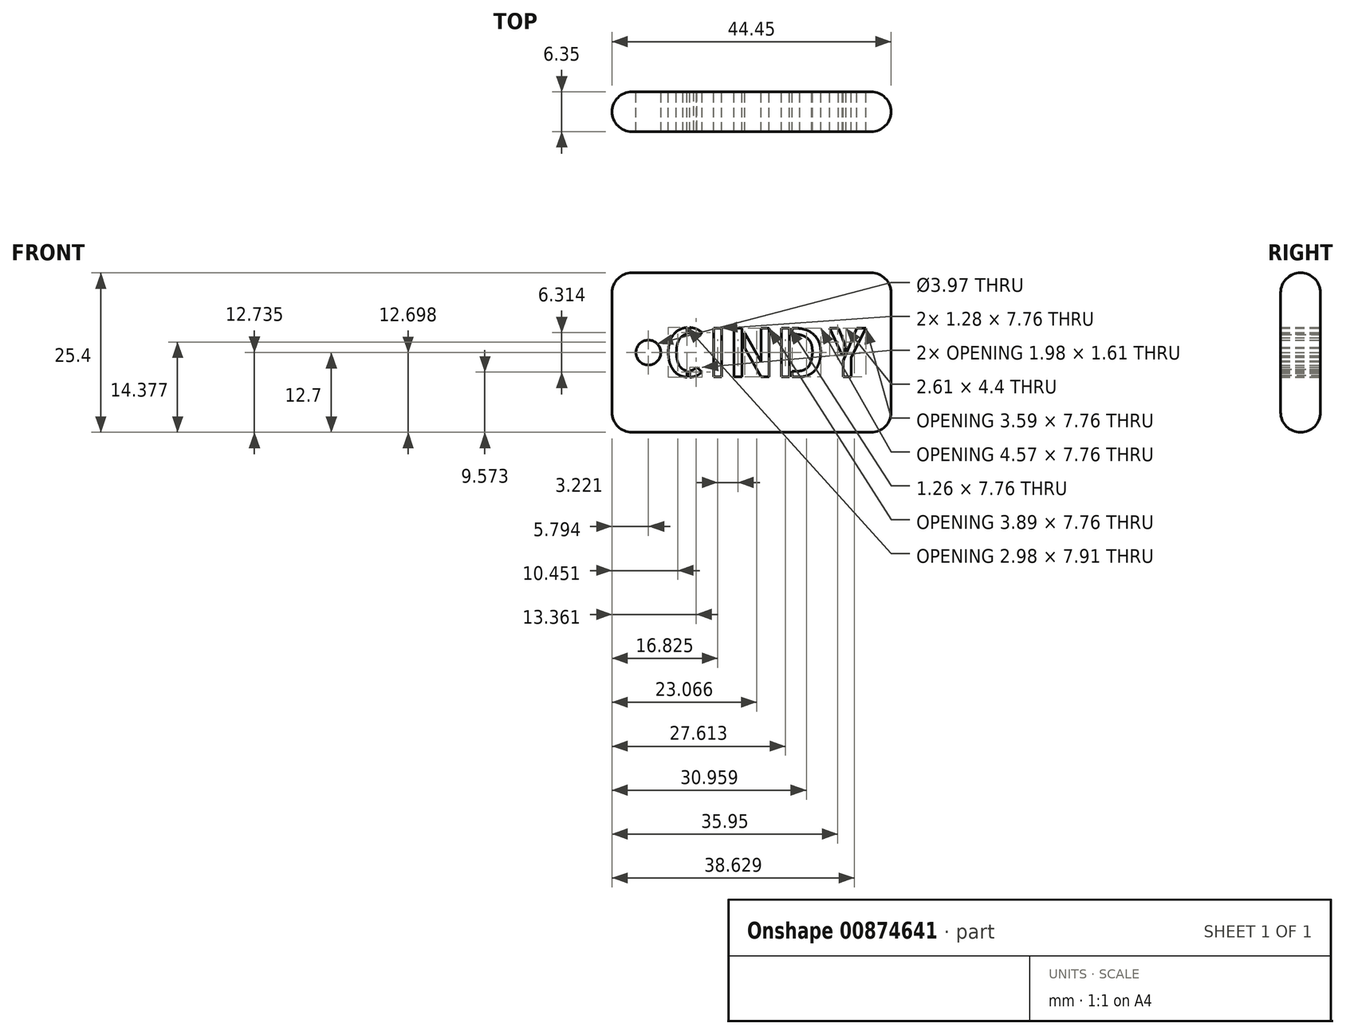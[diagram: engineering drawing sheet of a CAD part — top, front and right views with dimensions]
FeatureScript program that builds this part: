
annotation { "Feature Type Name" : "Feature", "Feature Type Description" : "" }
export const myFeature = defineFeature(function(context is Context, id is Id, definition is map)
    precondition{}
    {
        {
            var Q0;
            Q0=qCreatedBy(makeId("Front.planeOp"),FACE);
            var sketch = newSketch(context, id + "F0", { "sketchPlane" : qUnion([Q0])});
            skLineSegment(sketch, "E0.bottom", {"start": v(0, 0) * mm, "end": v(44.45, 0) * mm});
            skLineSegment(sketch, "E0.top", {"start": v(0, 25.4) * mm, "end": v(44.45, 25.4) * mm});
            skLineSegment(sketch, "E0.left", {"start": v(0, 0) * mm, "end": v(0, 25.4) * mm});
            skLineSegment(sketch, "E0.right", {"start": v(44.45, 0) * mm, "end": v(44.45, 25.4) * mm});
            skText(sketch, "E1", { "text": "CINDY\n", "fontName": "AllertaStencil-Regular.ttf"});
            skCircle(sketch, "E2", {"center": v(5.8, 12.7) * mm, "radius": 1.98 * mm});
            skPoint(sketch, "E3.visualSharp", {"position": v(44.45, 25.4) * mm});
            skLineSegment(sketch, "E3.filletArc", {"start": v(44.45, 25.4) * mm, "end": v(44.45, 25.4) * mm});
            skPoint(sketch, "E4.visualSharp", {"position": v(44.45, 0) * mm});
            skLineSegment(sketch, "E4.filletArc", {"start": v(44.45, 0) * mm, "end": v(44.45, 0) * mm});
            skPoint(sketch, "E5.visualSharp", {"position": v(0, 0) * mm});
            skLineSegment(sketch, "E5.filletArc", {"start": v(0, 0) * mm, "end": v(0, 0) * mm});
            skPoint(sketch, "E6.visualSharp", {"position": v(0, 25.4) * mm});
            skLineSegment(sketch, "E6.filletArc", {"start": v(0, 25.4) * mm, "end": v(0, 25.4) * mm});
            const initialGuessF0  = {"E1": [0.00813, 0.00882, 1, 0, 0.00776]};
            skSetInitialGuess(sketch, initialGuessF0);
            skSolve(sketch);
        }
        {
            var Q0;
            Q0=makeQuery(id+"F0.imprint","IMPRINT",FACE,{"disambiguationData":[TD([[makeQuery(id+"F0.imprint","IMPRINT",EDGE,{"derivedFrom":sQuery(id+"F0.wireOp",EDGE,"E0.bottom")}),1.0]])]});
            extrude(context, id + "F1", {"entities" : qUnion([Q0]), "depth" : 6.35 * mm, "offsetDistance" : 25.4 * mm});
        }
        {
            var Q0;
            Q0=makeQuery(id+"F1.opExtrude","CAP_EDGE",EDGE,{"disambiguationData":[OSD([sQuery(id+"F0.wireOp",EDGE,"E0.top")])],"isStart":false});
            var Q1;
            Q1=makeQuery(id+"F1.opExtrude","CAP_EDGE",EDGE,{"disambiguationData":[OSD([sQuery(id+"F0.wireOp",EDGE,"E0.bottom")])],"isStart":false});
            var Q2;
            Q2=makeQuery(id+"F1.opExtrude","CAP_EDGE",EDGE,{"disambiguationData":[OSD([sQuery(id+"F0.wireOp",EDGE,"E0.right")])],"isStart":false});
            var Q3;
            Q3=makeQuery(id+"F1.opExtrude","CAP_EDGE",EDGE,{"disambiguationData":[OSD([sQuery(id+"F0.wireOp",EDGE,"E0.left")])],"isStart":false});
            var Q4;
            Q4=makeQuery(id+"F1.opExtrude","CAP_EDGE",EDGE,{"disambiguationData":[OSD([sQuery(id+"F0.wireOp",EDGE,"E0.top")])],"isStart":true});
            var Q5;
            Q5=makeQuery(id+"F1.opExtrude","CAP_EDGE",EDGE,{"disambiguationData":[OSD([sQuery(id+"F0.wireOp",EDGE,"E0.right")])],"isStart":true});
            var Q6;
            Q6=makeQuery(id+"F1.opExtrude","CAP_EDGE",EDGE,{"disambiguationData":[OSD([sQuery(id+"F0.wireOp",EDGE,"E0.left")])],"isStart":true});
            var Q7;
            Q7=makeQuery(id+"F1.opExtrude","CAP_EDGE",EDGE,{"disambiguationData":[OSD([sQuery(id+"F0.wireOp",EDGE,"E0.bottom")])],"isStart":true});
            fillet(context, id + "F2", {"entities" : qUnion([Q0, Q1, Q2, Q3, Q4, Q5, Q6, Q7]), "radius" : 3.17 * mm, "tangentPropagation" : true, "allowEdgeOverflow" : false});
        }
        {
            var Q0;
            Q0=makeQuery(id+"F2.opFillet","BLEND_EDGE",EDGE,{"blendedFrom":[makeQuery(id+"F1.opExtrude","CAP_EDGE",EDGE,{"disambiguationData":[OSD([sQuery(id+"F0.wireOp",EDGE,"E0.bottom")])],"isStart":true}),makeQuery(id+"F1.opExtrude","CAP_EDGE",EDGE,{"disambiguationData":[OSD([sQuery(id+"F0.wireOp",EDGE,"E0.left")])],"isStart":true})],"blendedInto":[]});
            var Q1;
            Q1=makeQuery(id+"F2.opFillet","BLEND_EDGE",EDGE,{"blendedFrom":[makeQuery(id+"F1.opExtrude","CAP_EDGE",EDGE,{"disambiguationData":[OSD([sQuery(id+"F0.wireOp",EDGE,"E0.bottom")])],"isStart":true}),makeQuery(id+"F1.opExtrude","CAP_EDGE",EDGE,{"disambiguationData":[OSD([sQuery(id+"F0.wireOp",EDGE,"E0.right")])],"isStart":true})],"blendedInto":[]});
            var Q2;
            Q2=makeQuery(id+"F2.opFillet","BLEND_EDGE",EDGE,{"blendedFrom":[makeQuery(id+"F1.opExtrude","CAP_EDGE",EDGE,{"disambiguationData":[OSD([sQuery(id+"F0.wireOp",EDGE,"E0.top")])],"isStart":true}),makeQuery(id+"F1.opExtrude","CAP_EDGE",EDGE,{"disambiguationData":[OSD([sQuery(id+"F0.wireOp",EDGE,"E0.right")])],"isStart":true})],"blendedInto":[]});
            var Q3;
            Q3=makeQuery(id+"F2.opFillet","BLEND_EDGE",EDGE,{"blendedFrom":[makeQuery(id+"F1.opExtrude","CAP_EDGE",EDGE,{"disambiguationData":[OSD([sQuery(id+"F0.wireOp",EDGE,"E0.top")])],"isStart":true}),makeQuery(id+"F1.opExtrude","CAP_EDGE",EDGE,{"disambiguationData":[OSD([sQuery(id+"F0.wireOp",EDGE,"E0.left")])],"isStart":true})],"blendedInto":[]});
            fillet(context, id + "F3", {"entities" : qUnion([Q0, Q1, Q2, Q3]), "radius" : 3.17 * mm, "tangentPropagation" : true, "allowEdgeOverflow" : false});
        }
    });
